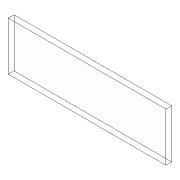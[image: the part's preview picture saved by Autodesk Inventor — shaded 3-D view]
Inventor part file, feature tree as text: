
AUTODESK INVENTOR PART (.ipt)
format: ipt  version: 2018.3 (Build 223284000, 284)  size: 73,216 bytes
history: native  units: in
note: dims shown in document units (in); Inventor stores cm internally (conversion verified against a paired STEP export)
features: extrude x1, sketch x1
ambient origin geometry x8: Origin, YZ Plane, XZ Plane, XY Plane, X Axis, Y Axis, Z Axis, Center Point
bodies: Solid1 (feature_tree)
feature tree (2):
  extrude  "Extrusion1"  Depth=0.675in
  sketch  "Sketch1"  dims[d0=2.19in d1=0.675in d2=0.08in d3=0.0in]
